# Revit family: NLRS_33_GM_FB_TC_STORAX_kooiladder_GL-VM-K
name_source: partatom
category: Generic Models
revit_build: Autodesk Revit 2015 (Build: 20140223_1515(x64)
units: mm (PartAtom-declared; Revit-internal decimal feet)

## types (1)
- GL-VM-K
    Default Elevation = 0 mm  [stored 0 ft]
    Manufacturer = Storax
    Model = DLL-VM
    URL = http://www.storax.nl
    aantal sporten = 13
    antislip profilering = Yes
    belasting totaal = 150.00 kg
    breedte ladderdeel 1 = 550 mm
    code productgroep = LUI
    conservering = brut
    doorlopende ladderboom = Yes
    false = No
    garantietermijn in jaren = 5
    geanodiseerd = Yes
    inhaakbeugel en weghangbakje = No
    lengte ladderdeel = 3250 mm  [stored 10.6627 ft]
    materiaal = bcb_aluminium
    modeler = Bouwconnect
    muurbeugels = Yes
    normering = EN ISO 14122
    omschrijving = gevelladder vloer- muurbevestiging met kooi
    productgroep = Dakluiken
    true = Yes
    uitloopleuning = Yes
    uitschuifbare leuning = No
    uitstapbordes = Yes
    voetplaten = Yes

note: [stored X ft] marks values corroborated as IEEE doubles in the binary element streams (Revit-internal decimal feet)

## geometry (parser evidence)
native form markers: Blend x4, Sweep x15
no freeform markers — native parametric forms only
